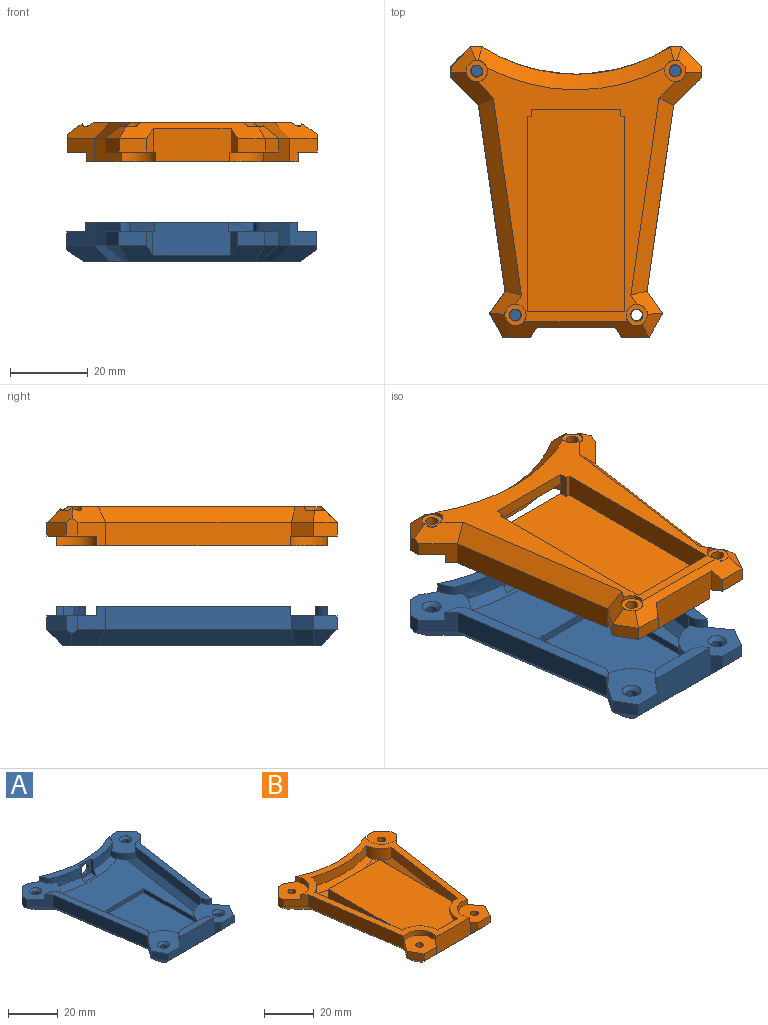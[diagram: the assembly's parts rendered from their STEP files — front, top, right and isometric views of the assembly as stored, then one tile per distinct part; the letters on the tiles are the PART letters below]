
ASSEMBLY  parts=2 mates=1
PART A: 147 faces, bbox 64.2x74.6x10.1 mm
  f0: plane 49.67x11.45mm, normal (0,0,1), area 145.6mm2, adj f1,f32,f33,f57,f70,f125,f131
  f1: cylinder r=6.87mm len=2.5mm, axis (0,0,1), area 0mm2, adj f0,f32,f56,f131
  f2: cylinder r=9.87mm len=10.08mm, axis (0,0,1), area 47.4mm2, adj f56,f62,f74,f80,f131
  f3: plane 19.05x3mm, normal (0,0,1), area 50.7mm2, adj f4,f36,f55,f62,f130,f132
  f4: cylinder r=6.83mm len=2.5mm, axis (0,0,1), area 1.5mm2, adj f3,f36,f54,f130
  f5: cylinder r=9.83mm len=10.03mm, axis (0,0,1), area 47.1mm2, adj f54,f62,f77,f79,f129
  f6: plane 49.74x11.46mm, normal (0,0,1), area 145.7mm2, adj f7,f34,f35,f53,f71,f128,f129
  f7: cylinder r=6.89mm len=2.5mm, axis (0,0,1), area 4.1mm2, adj f6,f34,f60,f128
  f8: cylinder r=9.89mm len=8.04mm, axis (0,0,1), area 31.8mm2, adj f11,f60,f63,f65,f77,f128
  f9: cylinder r=6.81mm len=2.5mm, axis (0,0,1), area 5.6mm2, adj f17,f37,f58,f126
  f10: cylinder r=9.81mm len=8.04mm, axis (0,0,1), area 31.6mm2, adj f58,f63,f64,f72,f74,f125
  f11: cylinder r=48mm len=12.8mm, axis (0,0,1), area 61mm2, adj f8,f17,f60,f63,f120,f127
  f12: plane 54.37x34.67mm, normal (0,0,-1), area 1264.6mm2, adj f94,f95,f96,f97,f102,f103,f104,f105
  f13: cylinder r=1.55mm len=3.1mm, axis (0,0,-1), area 4.9mm2, adj f38,f92
  f14: cylinder r=1.55mm len=3.1mm, axis (0,0,-1), area 4.9mm2, adj f38,f90
  f15: cylinder r=1.55mm len=3.1mm, axis (0,0,-1), area 4.9mm2, adj f38,f88
  f16: cylinder r=1.55mm len=3.1mm, axis (0,0,-1), area 4.9mm2, adj f38,f86
  f17: plane 39.39x7.49mm, normal (0,0,1), area 104.3mm2, adj f9,f11,f37,f59,f72,f120,f121,f122
  f18: plane 3.5x2.98mm, normal (0,1,0), area 10.4mm2, adj f19,f37,f42,f60
  f19: plane 4.95x4.95mm, normal (-0.71,0.71,0), area 24.5mm2, adj f18,f20,f44,f60
  f20: plane 4.56x3mm, normal (-1,0,0), area 12.1mm2, adj f19,f34,f44,f46,f60
  f21: plane 3.5x2.98mm, normal (0,1,0), area 10.4mm2, adj f23,f37,f39,f58
  f22: plane 4.56x3mm, normal (1,0,0), area 12.1mm2, adj f23,f33,f41,f43,f58
  f23: plane 4.95x4.95mm, normal (0.71,0.71,0), area 24.5mm2, adj f21,f22,f41,f58
  f24: plane 5.96x2.46mm, normal (-0.82,-0.57,0), area 14.2mm2, adj f25,f36,f51,f56
  f25: plane 7x3.5mm, normal (0,-1,0), area 24.5mm2, adj f24,f26,f51,f56
  f26: plane 6.06x3.5mm, normal (0.87,-0.5,0), area 24.5mm2, adj f25,f27,f49,f56
  f27: plane 5.73x4.02mm, normal (0.82,0.57,0), area 24.5mm2, adj f26,f32,f47,f56
  f28: plane 5.73x4.02mm, normal (-0.82,0.57,0), area 24.5mm2, adj f29,f35,f50,f54
  f29: plane 6.06x3.5mm, normal (-0.87,-0.5,0), area 24.5mm2, adj f28,f30,f52,f54
  f30: plane 7x3.5mm, normal (0,-1,0), area 24.5mm2, adj f29,f31,f51,f54
  f31: plane 5.96x2.46mm, normal (0.82,-0.57,0), area 14.2mm2, adj f30,f36,f51,f54
  f32: plane 47.66x6.79mm, normal (0.99,-0.14,0), area 288.3mm2, adj f0,f1,f27,f33,f45,f56
  f33: plane 7.07x7.07mm, normal (0.71,-0.71,0), area 42.9mm2, adj f0,f22,f32,f43,f57,f58
  f34: plane 7.07x7.07mm, normal (-0.71,-0.71,0), area 42.9mm2, adj f6,f7,f20,f35,f46,f60
  f35: plane 47.66x6.79mm, normal (-0.99,-0.14,0), area 288.5mm2, adj f6,f28,f34,f48,f53,f54
  f36: plane 20x8.46mm, normal (0,-1,0), area 166.8mm2, adj f3,f4,f24,f31,f51,f54,f55,f56
  f37: cylinder r=45mm len=48.27mm, axis (0,0,1), area 258.3mm2, adj f9,f17,f18,f21,f40,f58,f59,f60
  f38: plane 66.48x55.83mm, normal (0,0,-1), area 793.4mm2, adj f13,f14,f15,f16,f39,f40,f41,f42
  f39: plane 4.04x4.04mm, normal (0,0.71,-0.71), area 9mm2, adj f21,f38,f40,f41
  f40: cone r=49mm half-angle=45deg, axis (0,0,-1), area 294.3mm2, adj f37,f38,f39,f42,f124
  f41: plane 6.61x6.45mm, normal (0.5,0.5,-0.71), area 34mm2, adj f22,f23,f38,f39,f43
  f42: plane 4.04x4.04mm, normal (0,0.71,-0.71), area 9mm2, adj f18,f38,f40,f44
  f43: plane 10.84x8.57mm, normal (0.5,-0.5,-0.71), area 59.4mm2, adj f22,f33,f38,f41,f45
  f44: plane 6.61x6.45mm, normal (-0.5,0.5,-0.71), area 34mm2, adj f19,f20,f38,f42,f46
  f45: plane 50.55x10.98mm, normal (0.7,-0.1,-0.71), area 280.6mm2, adj f32,f38,f43,f47
  f46: plane 10.84x8.57mm, normal (-0.5,-0.5,-0.71), area 59.4mm2, adj f20,f34,f38,f44,f48
  f47: plane 8.2x5.94mm, normal (0.58,0.41,-0.71), area 36.9mm2, adj f27,f38,f45,f49
  f48: plane 50.55x10.98mm, normal (-0.7,-0.1,-0.71), area 280.6mm2, adj f35,f38,f46,f50
  f49: plane 6.06x5.81mm, normal (0.61,-0.35,-0.71), area 25.9mm2, adj f26,f38,f47,f51
  f50: plane 8.2x5.94mm, normal (-0.58,0.41,-0.71), area 36.9mm2, adj f28,f38,f48,f52
  f51: plane 37.44x4mm, normal (0,-0.71,-0.71), area 123.2mm2, adj f24,f25,f30,f31,f36,f38,f49,f52
  f52: plane 6.06x5.81mm, normal (-0.61,-0.35,-0.71), area 25.9mm2, adj f29,f38,f50,f51
  f53: cylinder r=6.83mm len=2.5mm, axis (0,0,1), area 0mm2, adj f6,f35,f54,f129
  f54: plane 16.64x15.47mm, normal (0,0,1), area 151.7mm2, adj f4,f5,f28,f29,f30,f31,f35,f36
  f55: cylinder r=6.87mm len=2.5mm, axis (0,0,1), area 1.5mm2, adj f3,f36,f56,f132
  f56: plane 16.65x15.54mm, normal (0,0,1), area 152.6mm2, adj f1,f2,f24,f25,f26,f27,f32,f36
  f57: cylinder r=6.81mm len=2.5mm, axis (0,0,1), area 4mm2, adj f0,f33,f58,f125
  f58: plane 16.32x15.41mm, normal (0,0,1), area 141.7mm2, adj f9,f10,f21,f22,f23,f33,f37,f57
  f59: cylinder r=6.89mm len=2.5mm, axis (0,0,1), area 5.1mm2, adj f17,f37,f60,f127
  f60: plane 16.46x15.45mm, normal (0,0,1), area 143.5mm2, adj f7,f8,f11,f18,f19,f20,f34,f37
  f61: plane 61.43x45.52mm, normal (0,0,1), area 1182.8mm2, adj f62,f63,f66,f67,f68,f69,f73,f74
  f62: plane 22.07x7mm, normal (0,1,0), area 95.4mm2, adj f2,f3,f5,f54,f56,f61,f68,f69
  f63: cone r=51.12mm half-angle=45deg, axis (0,0,-1), area 109.2mm2, adj f8,f10,f11,f61,f64,f65,f66,f67
  f64: plane 9.01x8.29mm, normal (0,0,-1), area 37.2mm2, adj f10,f63,f67,f73,f74
  f65: plane 9.03x8.46mm, normal (0,0,-1), area 38mm2, adj f8,f63,f66,f75,f77
  f66: cylinder r=4.55mm len=4.46mm, axis (0,0,-1), area 6.6mm2, adj f61,f63,f65,f75
  f67: cylinder r=4.55mm len=4.53mm, axis (0,0,-1), area 6.6mm2, adj f61,f63,f64,f73
  f68: cylinder r=4.55mm len=4.7mm, axis (0,0,-1), area 8.7mm2, adj f61,f62,f76,f80
  f69: cylinder r=4.55mm len=4.67mm, axis (0,0,-1), area 8.7mm2, adj f61,f62,f78,f79
  f70: plane 41.75x5.95mm, normal (-0.99,0.14,0), area 200.7mm2, adj f0,f74,f125,f131
  f71: plane 41.82x5.96mm, normal (0.99,0.14,0), area 200.9mm2, adj f6,f77,f128,f129
  f72: cylinder r=48mm len=12.86mm, axis (0,0,1), area 61.2mm2, adj f10,f17,f58,f63,f121,f126
  f73: plane 4.15x3.45mm, normal (-0.5,0.5,0.71), area 8mm2, adj f61,f64,f67,f74
  f74: plane 51.52x9.42mm, normal (-0.7,0.1,0.71), area 155.6mm2, adj f2,f10,f61,f64,f70,f73,f76,f80
  f75: plane 4.19x3.46mm, normal (0.5,0.5,0.71), area 8mm2, adj f61,f65,f66,f77
  f76: plane 2.1x1.54mm, normal (-0.58,-0.41,0.71), area 1.9mm2, adj f61,f68,f74,f80
  f77: plane 51.51x9.4mm, normal (0.7,0.1,0.71), area 155.6mm2, adj f5,f8,f61,f65,f71,f75,f78,f79
  f78: plane 2.12x1.54mm, normal (0.58,-0.41,0.71), area 2mm2, adj f61,f69,f77,f79
  f79: plane 10x9.21mm, normal (0,0,-1), area 55.5mm2, adj f5,f62,f69,f77,f78
  f80: plane 10.06x9.24mm, normal (0,0,-1), area 56.2mm2, adj f2,f62,f68,f74,f76
  f81: plane 32x2mm, normal (-1,0,0), area 64mm2, adj f61,f82,f84,f85
  f82: plane 22x2mm, normal (0,1,0), area 44mm2, adj f61,f81,f83,f85
  f83: plane 32x2mm, normal (1,0,0), area 64mm2, adj f61,f82,f84,f85
  f84: plane 22x2mm, normal (0,-1,0), area 44mm2, adj f61,f81,f83,f85
  f85: plane 32x22mm, normal (0,0,1), area 704mm2, adj f81,f82,f83,f84
  f86: plane 3.1x3.1mm, normal (0,0,-1), area 0.9mm2, adj f16,f87
  f87: cylinder r=1.45mm len=6mm, axis (0,0,1), area 54.7mm2, adj f86,f101
  f88: plane 3.1x3.1mm, normal (0,0,-1), area 0.9mm2, adj f15,f89
  f89: cylinder r=1.45mm len=6mm, axis (0,0,1), area 54.7mm2, adj f88,f100
  f90: plane 3.1x3.1mm, normal (0,0,-1), area 0.9mm2, adj f14,f91
  f91: cylinder r=1.45mm len=6mm, axis (0,0,1), area 54.7mm2, adj f90,f99
  f92: plane 3.1x3.1mm, normal (0,0,-1), area 0.9mm2, adj f13,f93
  f93: cylinder r=1.45mm len=6mm, axis (0,0,1), area 54.7mm2, adj f92,f98
  f94: plane 19.17x0.25mm, normal (0,1,0), area 4.8mm2, adj f12,f38,f95,f97
  f95: plane 54.37x7.75mm, normal (-0.99,0.14,0), area 13.7mm2, adj f12,f38,f94,f96
  f96: cylinder r=53mm len=34.67mm, axis (0,0,-1), area 8.8mm2, adj f12,f38,f95,f97
  f97: plane 54.37x7.75mm, normal (0.99,0.14,0), area 13.7mm2, adj f12,f38,f94,f96
  f98: cone r=1.45mm half-angle=45deg, axis (0,0,1), area 17.3mm2, adj f54,f93
  f99: cone r=1.45mm half-angle=45deg, axis (0,0,1), area 17.3mm2, adj f56,f91
  f100: cone r=1.45mm half-angle=45deg, axis (0,0,1), area 17.3mm2, adj f58,f89
  f101: cone r=1.45mm half-angle=45deg, axis (0,0,1), area 17.3mm2, adj f60,f87
  f102: plane 3x1.73mm, normal (0.87,0.5,0), area 0.9mm2, adj f12,f103,f110,f111
  f103: plane 16.38x0.25mm, normal (0,-1,0), area 4.1mm2, adj f12,f102,f104,f111
  f104: plane 17.42x10.06mm, normal (-0.87,0.5,0), area 5mm2, adj f12,f103,f105,f111
  f105: plane 2.89x0.25mm, normal (0,1,0), area 0.7mm2, adj f12,f104,f106,f111
  f106: plane 8.71x5.03mm, normal (0.87,0.5,0), area 2.5mm2, adj f12,f105,f107,f111
  f107: plane 2.99x1.74mm, normal (0.86,-0.5,0), area 0.9mm2, adj f12,f106,f108,f111
  f108: plane 8.2x4.73mm, normal (-0.87,-0.5,0), area 2.4mm2, adj f12,f107,f109,f111
  f109: plane 10.92x6.3mm, normal (0.87,-0.5,0), area 3.2mm2, adj f12,f108,f110,f111
  f110: plane 9.46x0.25mm, normal (0,1,0), area 2.4mm2, adj f12,f102,f109,f111
  f111: plane 17.97x17.42mm, normal (0,0,-1), area 122.2mm2, adj f102,f103,f104,f105,f106,f107,f108,f109
  f112: plane 3x1.73mm, normal (-0.87,0.5,0), area 0.9mm2, adj f12,f113,f117,f118
  f113: plane 1.5x0.87mm, normal (0.87,0.5,0), area 0.4mm2, adj f12,f112,f114,f118
  f114: plane 1.5x0.87mm, normal (0.87,-0.5,0), area 0.4mm2, adj f12,f113,f115,f118
  f115: plane 3x1.73mm, normal (0.87,0.5,0), area 0.9mm2, adj f12,f114,f116,f118
  f116: plane 1.73x0.25mm, normal (0,-1,0), area 0.4mm2, adj f12,f115,f117,f118
  f117: plane 3x1.73mm, normal (-0.87,-0.5,0), area 0.9mm2, adj f12,f112,f116,f118
  f118: plane 6x3.46mm, normal (0,0,-1), area 9.1mm2, adj f112,f113,f114,f115,f116,f117
  f119: plane 7.01x0.63mm, normal (0,1,0), area 4.1mm2, adj f63,f120,f121,f123
  f120: plane 7x3.23mm, normal (1,0,0), area 12.8mm2, adj f11,f17,f63,f119,f122,f123
  f121: plane 7x3.23mm, normal (-1,0,0), area 12.8mm2, adj f17,f63,f72,f119,f122,f123
  f122: plane 7x7mm, normal (0,-1,0), area 26.9mm2, adj f17,f120,f121,f123,f124
  f123: plane 7x3.23mm, normal (0,0,1), area 22.6mm2, adj f119,f120,f121,f122
  f124: cylinder r=2.65mm len=5.3mm, axis (0,-1,0), area 23.5mm2, adj f37,f40,f122
  f125: cylinder r=4mm len=4.76mm, axis (0,0,1), area 16.5mm2, adj f0,f10,f57,f58,f70,f74
  f126: cylinder r=4mm len=2.7mm, axis (0,0,1), area 9.5mm2, adj f9,f17,f58,f72
  f127: cylinder r=4mm len=2.77mm, axis (0,0,-1), area 9.7mm2, adj f11,f17,f59,f60
  f128: cylinder r=4mm len=4.76mm, axis (0,0,1), area 16.3mm2, adj f6,f7,f8,f60,f71,f77
  f129: cylinder r=4mm len=4.76mm, axis (0,0,1), area 14.8mm2, adj f5,f6,f53,f54,f71,f77
  f130: cylinder r=4mm len=3.69mm, axis (0,0,1), area 11.7mm2, adj f3,f4,f54,f62
  f131: cylinder r=4mm len=4.76mm, axis (0,0,1), area 14.8mm2, adj f0,f1,f2,f56,f70,f74
  f132: cylinder r=4mm len=3.69mm, axis (0,0,1), area 11.7mm2, adj f3,f55,f56,f62
  f133: cylinder r=4.05mm len=0.97mm, axis (0,0,-1), area 0.2mm2, adj f134,f135,f137
  f134: plane 0.53x0.33mm, normal (-0.5,0.5,0.71), area 0mm2, adj f133,f135,f136,f137
  f135: plane 0.97x0.1mm, normal (0,0,-1), area 0mm2, adj f133,f134,f136,f137
  f136: plane 0.83x0.29mm, normal (-1,0,0), area 0.1mm2, adj f134,f135,f137
  f137: plane 0.46x0.33mm, normal (-0.5,-0.5,0.71), area 0mm2, adj f133,f134,f135,f136
  f138: plane 1.14x0.21mm, normal (0,0,-1), area 0.1mm2, adj f139,f140,f141,f142
  f139: plane 0.53x0.38mm, normal (0.5,-0.5,0.71), area 0.1mm2, adj f138,f140,f141,f142
  f140: cylinder r=4.05mm len=1.14mm, axis (0,0,-1), area 0.2mm2, adj f138,f139,f142
  f141: plane 0.83x0.29mm, normal (1,0,0), area 0.1mm2, adj f138,f139,f142
  f142: plane 0.64x0.39mm, normal (0.5,0.5,0.71), area 0.1mm2, adj f138,f139,f140,f141
  f143: plane 0.08x0.06mm, normal (0,0,-1), area 0mm2, adj f144,f145,f146
  f144: plane 0.06x0.06mm, normal (0.82,0.57,0), area 0mm2, adj f143,f145,f146
  f145: plane 0.08x0.06mm, normal (0,0.71,0.71), area 0mm2, adj f143,f144,f146
  f146: cylinder r=4.05mm len=0.08mm, axis (0,0,-1), area 0mm2, adj f143,f144,f145
PART B: 115 faces, bbox 64.2x74.5x10.1 mm
  f0: plane 6x1mm, normal (0,-1,0), area 6mm2, adj f3,f71,f78,f92
  f1: cylinder r=9.83mm len=10.02mm, axis (0,0,1), area 35.4mm2, adj f20,f22,f24,f26,f63,f74,f91
  f2: cylinder r=9.87mm len=10.08mm, axis (0,0,1), area 35.6mm2, adj f22,f23,f25,f26,f62,f73,f91
  f3: plane 65.13x50.87mm, normal (0,0,-1), area 860.7mm2, adj f0,f4,f7,f8,f9,f11,f15,f47
  f4: cone r=49mm half-angle=45deg, axis (0,0,-1), area 289.6mm2, adj f3,f5,f13,f46,f83,f90
  f5: plane 3.45x3.45mm, normal (0,0.71,-0.71), area 8.6mm2, adj f4,f6,f27,f90
  f6: plane 6.5x6.42mm, normal (-0.5,0.5,-0.71), area 29.4mm2, adj f5,f7,f28,f29,f82,f90
  f7: plane 10.84x8.57mm, normal (-0.5,-0.5,-0.71), area 56.6mm2, adj f3,f6,f29,f43,f48,f90
  f8: plane 37.48x4.04mm, normal (0,-0.71,-0.71), area 115.7mm2, adj f3,f10,f12,f33,f34,f39,f40,f45
  f9: plane 8.26x5.97mm, normal (-0.58,0.41,-0.71), area 33mm2, adj f3,f10,f37,f48,f81,f87,f89
  f10: plane 6.09x5.39mm, normal (-0.61,-0.35,-0.71), area 22.2mm2, adj f8,f9,f38,f81,f88,f89
  f11: plane 8.24x5.95mm, normal (0.58,0.41,-0.71), area 32.9mm2, adj f3,f12,f36,f47,f80,f84,f86
  f12: plane 6.09x5.4mm, normal (0.61,-0.35,-0.71), area 22.2mm2, adj f8,f11,f35,f80,f84,f85
  f13: plane 3.52x3.52mm, normal (0,0.71,-0.71), area 8.7mm2, adj f4,f14,f30,f83
  f14: plane 6.51x6.45mm, normal (0.5,0.5,-0.71), area 29.3mm2, adj f13,f15,f31,f32,f79,f83
  f15: plane 10.84x8.57mm, normal (0.5,-0.5,-0.71), area 56.1mm2, adj f3,f14,f31,f42,f47,f83
  f16: cylinder r=1.55mm len=6.5mm, axis (0,0,-1), area 63.3mm2, adj f56,f82
  f17: cylinder r=1.55mm len=6.5mm, axis (0,0,-1), area 63.3mm2, adj f50,f81
  f18: cylinder r=1.55mm len=6.5mm, axis (0,0,-1), area 63.3mm2, adj f52,f80
  f19: cylinder r=1.55mm len=6.5mm, axis (0,0,-1), area 63.3mm2, adj f54,f79
  f20: plane 3.13x0.45mm, normal (0,0,-1), area 0.7mm2, adj f1,f24,f74
  f21: plane 45.52x43.94mm, normal (0,0,1), area 396.8mm2, adj f23,f24,f57,f60,f61,f65,f66,f73
  f22: plane 11.46x2mm, normal (0,1,0), area 22.9mm2, adj f1,f2,f26,f91
  f23: plane 49.61x7.43mm, normal (-0.7,0.1,0.71), area 140.6mm2, adj f2,f21,f25,f58,f62,f65,f67,f73
  f24: plane 49.61x7.42mm, normal (0.7,0.1,0.71), area 140.6mm2, adj f1,f20,f21,f59,f63,f66,f68,f74
  f25: plane 3.2x0.46mm, normal (0,0,-1), area 0.7mm2, adj f2,f23,f73
  f26: plane 69.62x54.44mm, normal (0,0,1), area 607.3mm2, adj f1,f2,f22,f41,f42,f43,f44,f45
  f27: plane 3.5x2.98mm, normal (0,1,0), area 10.4mm2, adj f5,f28,f46,f56
  f28: plane 4.95x4.95mm, normal (-0.71,0.71,0), area 24.5mm2, adj f6,f27,f29,f56
  f29: plane 4.56x3mm, normal (-1,0,0), area 12.1mm2, adj f6,f7,f28,f43,f56
  f30: plane 3.5x2.98mm, normal (0,1,0), area 10.4mm2, adj f13,f32,f46,f54
  f31: plane 4.56x3mm, normal (1,0,0), area 12.1mm2, adj f14,f15,f32,f42,f54
  f32: plane 4.95x4.95mm, normal (0.71,0.71,0), area 24.5mm2, adj f14,f30,f31,f54
  f33: plane 5.96x2.46mm, normal (-0.82,-0.57,0), area 14.2mm2, adj f8,f34,f45,f52
  f34: plane 7x3.5mm, normal (0,-1,0), area 24.5mm2, adj f8,f33,f35,f52
  f35: plane 6.06x3.5mm, normal (0.87,-0.5,0), area 24.5mm2, adj f12,f34,f36,f52
  f36: plane 5.73x4.02mm, normal (0.82,0.57,0), area 24.5mm2, adj f11,f35,f41,f52
  f37: plane 5.73x4.02mm, normal (-0.82,0.57,0), area 24.5mm2, adj f9,f38,f44,f50
  f38: plane 6.06x3.5mm, normal (-0.87,-0.5,0), area 24.5mm2, adj f10,f37,f39,f50
  f39: plane 7x3.5mm, normal (0,-1,0), area 24.5mm2, adj f8,f38,f40,f50
  f40: plane 5.96x2.46mm, normal (0.82,-0.57,0), area 14.2mm2, adj f8,f39,f45,f50
  f41: plane 47.66x6.79mm, normal (0.99,-0.14,0), area 288.3mm2, adj f26,f36,f42,f47,f51,f52
  f42: plane 7.07x7.07mm, normal (0.71,-0.71,0), area 42.9mm2, adj f15,f26,f31,f41,f53,f54
  f43: plane 7.07x7.07mm, normal (-0.71,-0.71,0), area 42.9mm2, adj f7,f26,f29,f44,f55,f56
  f44: plane 47.66x6.79mm, normal (-0.99,-0.14,0), area 288.5mm2, adj f26,f37,f43,f48,f49,f50
  f45: plane 20x8.46mm, normal (0,-1,0), area 166.8mm2, adj f8,f26,f33,f40,f49,f50,f51,f52
  f46: cylinder r=45mm len=48.27mm, axis (0,0,1), area 280.3mm2, adj f4,f26,f27,f30,f53,f54,f55,f56
  f47: plane 50.55x10.98mm, normal (0.7,-0.1,-0.71), area 280.6mm2, adj f3,f11,f15,f41
  f48: plane 50.55x10.98mm, normal (-0.7,-0.1,-0.71), area 280.6mm2, adj f3,f7,f9,f44
  f49: cylinder r=6.83mm len=10.02mm, axis (0,0,1), area 41.9mm2, adj f26,f44,f45,f50
  f50: plane 13.48x12.47mm, normal (0,0,1), area 119.3mm2, adj f17,f37,f38,f39,f40,f44,f45,f49
  f51: cylinder r=6.87mm len=10.08mm, axis (0,0,1), area 42.1mm2, adj f26,f41,f45,f52
  f52: plane 13.5x12.54mm, normal (0,0,1), area 120mm2, adj f18,f33,f34,f35,f36,f41,f45,f51
  f53: cylinder r=6.81mm len=10.62mm, axis (0,0,1), area 41.2mm2, adj f26,f42,f46,f54
  f54: plane 13.39x13.02mm, normal (0,0,1), area 122mm2, adj f19,f30,f31,f32,f42,f46,f53
  f55: cylinder r=6.89mm len=10.48mm, axis (0,0,1), area 41.1mm2, adj f26,f43,f46,f56
  f56: plane 13.54x13.04mm, normal (0,0,1), area 123.6mm2, adj f16,f27,f28,f29,f43,f46,f55
  f57: cone r=51.12mm half-angle=45deg, axis (0,0,-1), area 125.6mm2, adj f21,f58,f59,f60,f61,f64,f67,f68
  f58: plane 9.01x8.29mm, normal (0,0,-1), area 37.2mm2, adj f23,f57,f61,f65,f67
  f59: plane 9.03x8.46mm, normal (0,0,-1), area 38mm2, adj f24,f57,f60,f66,f68
  f60: cylinder r=4.55mm len=4.46mm, axis (0,0,-1), area 6.6mm2, adj f21,f57,f59,f66
  f61: cylinder r=4.55mm len=4.53mm, axis (0,0,-1), area 6.6mm2, adj f21,f57,f58,f65
  f62: plane 43.59x6.21mm, normal (-0.99,0.14,0), area 209.5mm2, adj f2,f23,f26,f67
  f63: plane 43.61x6.22mm, normal (0.99,0.14,0), area 209.6mm2, adj f1,f24,f26,f68
  f64: cylinder r=48mm len=31.36mm, axis (0,0,1), area 152mm2, adj f26,f57,f67,f68
  f65: plane 4.15x3.45mm, normal (-0.5,0.5,0.71), area 8mm2, adj f21,f23,f58,f61
  f66: plane 4.19x3.46mm, normal (0.5,0.5,0.71), area 8mm2, adj f21,f24,f59,f60
  f67: cylinder r=9.81mm len=7.99mm, axis (0,0,1), area 57.8mm2, adj f23,f26,f57,f58,f62,f64
  f68: cylinder r=9.89mm len=7.99mm, axis (0,0,1), area 58.2mm2, adj f24,f26,f57,f59,f63,f64
  f69: plane 50x6mm, normal (1,0,0), area 300mm2, adj f3,f70,f72,f92
  f70: plane 25x6mm, normal (0,1,0), area 150mm2, adj f3,f69,f71,f92
  f71: plane 50x6mm, normal (-1,0,0), area 300mm2, adj f0,f3,f70,f92
  f72: plane 6x1mm, normal (0,-1,0), area 6mm2, adj f3,f69,f77,f92
  f73: plane 46.18x5mm, normal (1,0,0), area 211.9mm2, adj f2,f21,f23,f25,f75,f91
  f74: plane 46.18x5mm, normal (-1,0,0), area 212.1mm2, adj f1,f20,f21,f24,f75,f91
  f75: plane 29x5mm, normal (0,1,0), area 76mm2, adj f21,f73,f74,f77,f78,f91,f92
  f76: plane 23x3mm, normal (0,-1,0), area 69mm2, adj f3,f21,f77,f78
  f77: plane 6x2mm, normal (1,0,0), area 12mm2, adj f3,f72,f75,f76,f92
  f78: plane 6x2mm, normal (-1,0,0), area 12mm2, adj f0,f3,f75,f76,f92
  f79: plane 5.5x5.5mm, normal (0,0,-1), area 15.9mm2, adj f14,f19,f83
  f80: plane 5.5x5.42mm, normal (0,0,-1), area 15.8mm2, adj f8,f11,f12,f18,f84,f85,f86
  f81: plane 5.5x5.39mm, normal (0,0,-1), area 15.8mm2, adj f8,f9,f10,f17,f87,f88,f89
  f82: plane 5.5x5.5mm, normal (0,0,-1), area 15.9mm2, adj f6,f16,f90
  f83: cylinder r=2.75mm len=5.5mm, axis (0,0,1), area 9.1mm2, adj f3,f4,f13,f14,f15,f79
  f84: cylinder r=2.75mm len=1.32mm, axis (0,0,1), area 0.2mm2, adj f11,f12,f80
  f85: cylinder r=2.75mm len=1.05mm, axis (0,0,1), area 0.1mm2, adj f8,f12,f80
  f86: cylinder r=2.75mm len=5.42mm, axis (0,0,1), area 7.7mm2, adj f3,f8,f11,f80
  f87: cylinder r=2.75mm len=5.39mm, axis (0,0,1), area 7.8mm2, adj f3,f8,f9,f81
  f88: cylinder r=2.75mm len=0.93mm, axis (0,0,1), area 0.1mm2, adj f8,f10,f81
  f89: cylinder r=2.75mm len=1.45mm, axis (0,0,1), area 0.2mm2, adj f9,f10,f81
  f90: cylinder r=2.75mm len=5.5mm, axis (0,0,1), area 9.1mm2, adj f3,f4,f5,f6,f7,f82
  f91: plane 53.04x29mm, normal (0,0,1), area 1403.6mm2, adj f1,f2,f22,f73,f74,f75
  f92: plane 52x25mm, normal (0,0,-1), area 1296mm2, adj f0,f69,f70,f71,f72,f75,f77,f78
  f93: plane 0.5x0.29mm, normal (-1,0,0), area 0.1mm2, adj f94,f95,f96
  f94: plane 0.5x0.31mm, normal (0.58,-0.41,0.71), area 0.1mm2, adj f93,f95,f96
  f95: plane 0.5x0.31mm, normal (0,0,-1), area 0.1mm2, adj f93,f94,f96
  f96: cylinder r=4.55mm len=0.31mm, axis (0,0,-1), area 0mm2, adj f93,f94,f95
  f97: plane 0.47x0.27mm, normal (1,0,0), area 0.1mm2, adj f98,f99,f100
  f98: plane 0.47x0.29mm, normal (0,0,-1), area 0.1mm2, adj f97,f99,f100
  f99: plane 0.47x0.29mm, normal (-0.58,-0.41,0.71), area 0.1mm2, adj f97,f98,f100
  f100: cylinder r=4.55mm len=0.29mm, axis (0,0,-1), area 0mm2, adj f97,f98,f99
  f101: cylinder r=4.05mm len=0.97mm, axis (0,0,-1), area 0.2mm2, adj f102,f103,f105
  f102: plane 0.53x0.33mm, normal (-0.5,0.5,0.71), area 0mm2, adj f101,f103,f104,f105
  f103: plane 0.97x0.1mm, normal (0,0,-1), area 0mm2, adj f101,f102,f104,f105
  f104: plane 0.83x0.29mm, normal (-1,0,0), area 0.1mm2, adj f102,f103,f105
  f105: plane 0.46x0.33mm, normal (-0.5,-0.5,0.71), area 0mm2, adj f101,f102,f103,f104
  f106: plane 1.14x0.21mm, normal (0,0,-1), area 0.1mm2, adj f107,f108,f109,f110
  f107: plane 0.53x0.38mm, normal (0.5,-0.5,0.71), area 0.1mm2, adj f106,f108,f109,f110
  f108: cylinder r=4.05mm len=1.14mm, axis (0,0,-1), area 0.2mm2, adj f106,f107,f110
  f109: plane 0.83x0.29mm, normal (1,0,0), area 0.1mm2, adj f106,f107,f110
  f110: plane 0.64x0.39mm, normal (0.5,0.5,0.71), area 0.1mm2, adj f106,f107,f108,f109
  f111: plane 0.08x0.06mm, normal (0,0,-1), area 0mm2, adj f112,f113,f114
  f112: plane 0.06x0.06mm, normal (0.82,0.57,0), area 0mm2, adj f111,f113,f114
  f113: plane 0.08x0.06mm, normal (0,0.71,0.71), area 0mm2, adj f111,f112,f114
  f114: cylinder r=4.05mm len=0.08mm, axis (0,0,-1), area 0mm2, adj f111,f112,f113
PLACE A t=(13.71,-39.11,2.6)mm fixed
PLACE B rot(axis=(0,1,0),180deg) t=(-6.22,-39.18,38.1)mm
MATE slider B.f16 <-> A.f9  axis (0,0,1) through (29.2,26.69,30.6)mm
